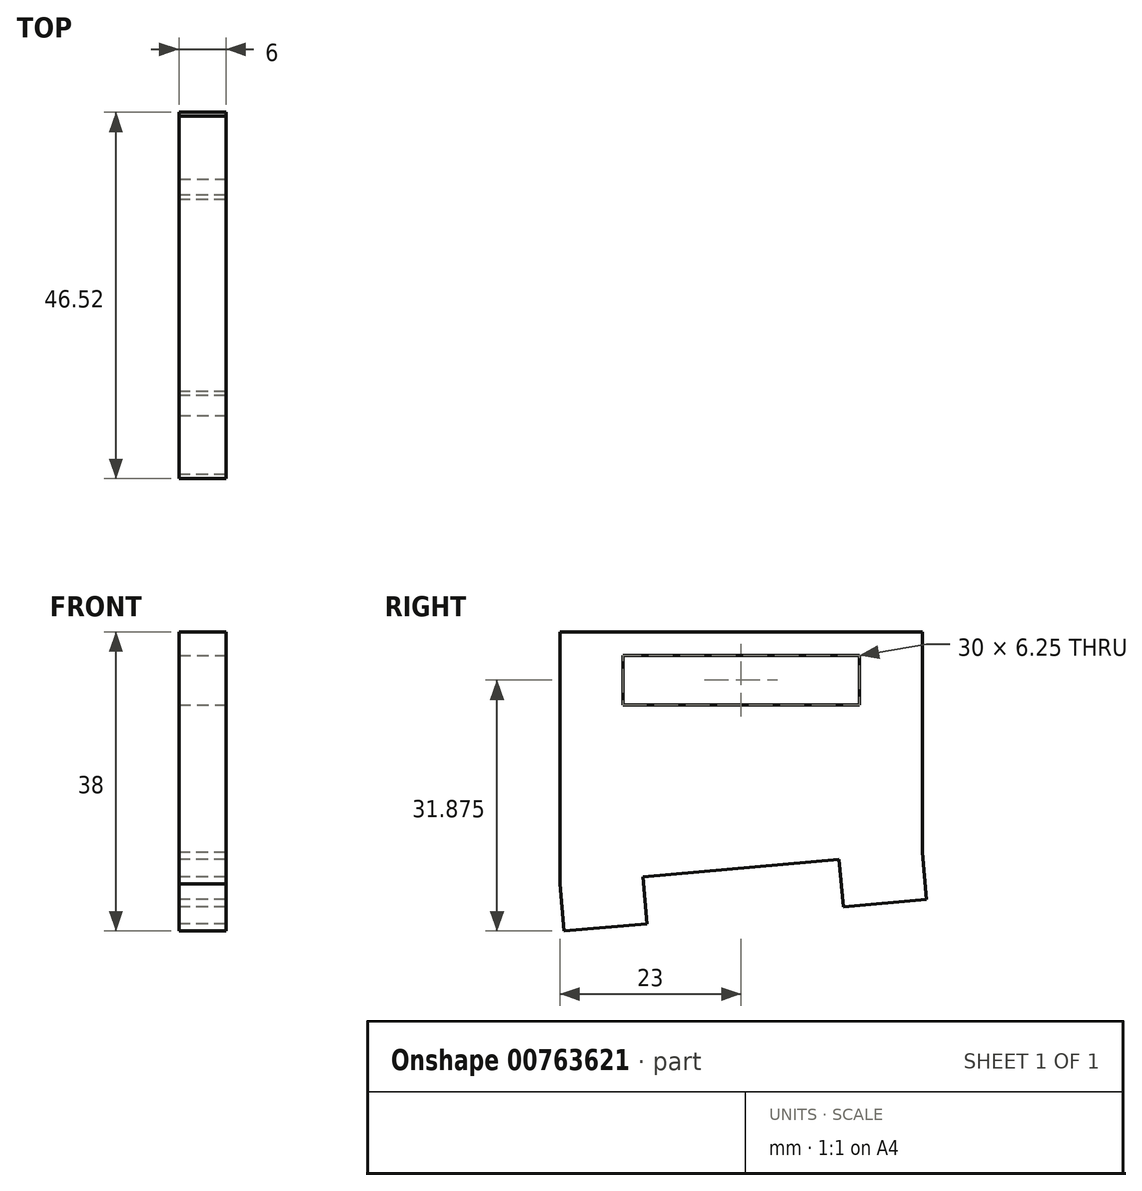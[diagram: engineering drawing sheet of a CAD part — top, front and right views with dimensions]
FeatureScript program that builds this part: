
annotation { "Feature Type Name" : "Feature", "Feature Type Description" : "" }
export const myFeature = defineFeature(function(context is Context, id is Id, definition is map)
    precondition{}
    {
        {
            var Q0;
            Q0=qCreatedBy(makeId("Right.planeOp"),FACE);
            var sketch = newSketch(context, id + "F0", { "sketchPlane" : qUnion([Q0])});
            skLineSegment(sketch, "E0.top", {"start": v(23, 0) * mm, "end": v(-23, 0) * mm});
            skLineSegment(sketch, "E0.left", {"start": v(23, -28) * mm, "end": v(23, 0) * mm});
            skLineSegment(sketch, "E0.right", {"start": v(-23, -32.02) * mm, "end": v(-23, 0) * mm});
            skPoint(sketch, "E0.middle", {"position": v(0, 0) * mm});
            skLineSegment(sketch, "E1", {"start": v(-23, -32.02) * mm, "end": v(23, -28) * mm});
            skLineSegment(sketch, "E2", {"start": v(23, -28) * mm, "end": v(-23, -28) * mm, "construction": true});
            skSolve(sketch);
        }
        {
            var Q0;
            Q0=qSketchRegion(id+"F0",true);
            extrude(context, id + "F1", {"entities" : qUnion([Q0]), "endBound" : BoundingType.SYMMETRIC, "depth" : 6 * mm, "offsetDistance" : 25 * mm});
        }
        {
            var Q0;
            Q0=qCreatedBy(makeId("Right.planeOp"),FACE);
            var sketch = newSketch(context, id + "F2", { "sketchPlane" : qUnion([Q0])});
            skLineSegment(sketch, "E3", {"start": v(-22.48, -38) * mm, "end": v(-11.93, -37.08) * mm});
            skLineSegment(sketch, "E4", {"start": v(-11.93, -37.08) * mm, "end": v(-12.45, -31.1) * mm});
            skLineSegment(sketch, "E5", {"start": v(-12.45, -31.1) * mm, "end": v(-23, -32.02) * mm});
            skLineSegment(sketch, "E6", {"start": v(-23, -32.02) * mm, "end": v(-22.48, -38) * mm});
            skLineSegment(sketch, "E7", {"start": v(0, -30.01) * mm, "end": v(0.68, -37.82) * mm, "construction": true});
            skLineSegment(sketch, "E8.MirrorCS", {"start": v(23, -28) * mm, "end": v(23.52, -33.98) * mm});
            skLineSegment(sketch, "E9.MirrorCS", {"start": v(12.45, -28.92) * mm, "end": v(23, -28) * mm});
            skLineSegment(sketch, "E10.MirrorCS", {"start": v(12.98, -34.9) * mm, "end": v(12.45, -28.92) * mm});
            skLineSegment(sketch, "E11.MirrorCS", {"start": v(23.52, -33.98) * mm, "end": v(12.98, -34.9) * mm});
            skSolve(sketch);
        }
        {
            var Q0;
            Q0=qSketchRegion(id+"F2",true);
            extrude(context, id + "F3", {"entities" : qUnion([Q0]), "operationType" : NewBodyOperationType.ADD, "endBound" : BoundingType.SYMMETRIC, "depth" : 6 * mm, "offsetDistance" : 25 * mm});
        }
        {
            var Q0;
            {var subQ0=sQuery(id+"F0.wireOp",EDGE,"E1");var subQ1=sQuery(id+"F0.wireOp",EDGE,"E0.right");var subQ2=sQuery(id+"F0.wireOp",EDGE,"E0.left");var subQ3=sQuery(id+"F0.wireOp",EDGE,"E0.top");Q0=makeQuery(id+"FRKY4pzqr8ala3Q_1.boolean.opBoolean","MERGE",FACE,{"derivedFrom":[makeQuery(id+"F1.opExtrude","CAP_FACE",FACE,{"disambiguationData":[OSD([subQ3,subQ2,subQ1,subQ0])],"isStart":false}),makeQuery(id+"FRKY4pzqr8ala3Q_1.opExtrude","CAP_FACE",FACE,{"disambiguationData":[OSD([subQ3,subQ2,subQ1,subQ0]),OD(0.0)],"isStart":false}),makeQuery(id+"FRKY4pzqr8ala3Q_1.opExtrude","CAP_FACE",FACE,{"disambiguationData":[OSD([subQ3,subQ2,subQ1,subQ0]),OD(1.0)],"isStart":false})]});}
            var sketch = newSketch(context, id + "F4", { "sketchPlane" : qUnion([Q0])});
            skLineSegment(sketch, "E12.bottom", {"start": v(15, -9.25) * mm, "end": v(-15, -9.25) * mm});
            skLineSegment(sketch, "E12.top", {"start": v(15, -3) * mm, "end": v(-15, -3) * mm});
            skLineSegment(sketch, "E12.left", {"start": v(15, -9.25) * mm, "end": v(15, -3) * mm});
            skLineSegment(sketch, "E12.right", {"start": v(-15, -9.25) * mm, "end": v(-15, -3) * mm});
            skPoint(sketch, "E12.middle", {"position": v(0, -6.12) * mm});
            skSolve(sketch);
        }
        {
            var Q0;
            Q0=makeQuery(id+"F4.imprint","IMPRINT",FACE,{"disambiguationData":[TD([[makeQuery(id+"F4.imprint","IMPRINT",EDGE,{"derivedFrom":sQuery(id+"F4.wireOp",EDGE,"E12.bottom")}),-1.0]])]});
            var Q1;
            Q1=makeQuery(id+"F1.opExtrude","CAP_FACE",FACE,{"disambiguationData":[OSD([sQuery(id+"F0.wireOp",EDGE,"E0.top"),sQuery(id+"F0.wireOp",EDGE,"E0.left"),sQuery(id+"F0.wireOp",EDGE,"E0.right"),sQuery(id+"F0.wireOp",EDGE,"E1")])],"isStart":true});
            extrude(context, id + "F5", {"entities" : qUnion([Q0]), "operationType" : NewBodyOperationType.REMOVE, "endBound" : BoundingType.UP_TO_NEXT, "oppositeDirection" : true, "depth" : 6 * mm, "endBoundEntityFace" : qUnion([Q1]), "offsetDistance" : 25 * mm});
        }
    });
